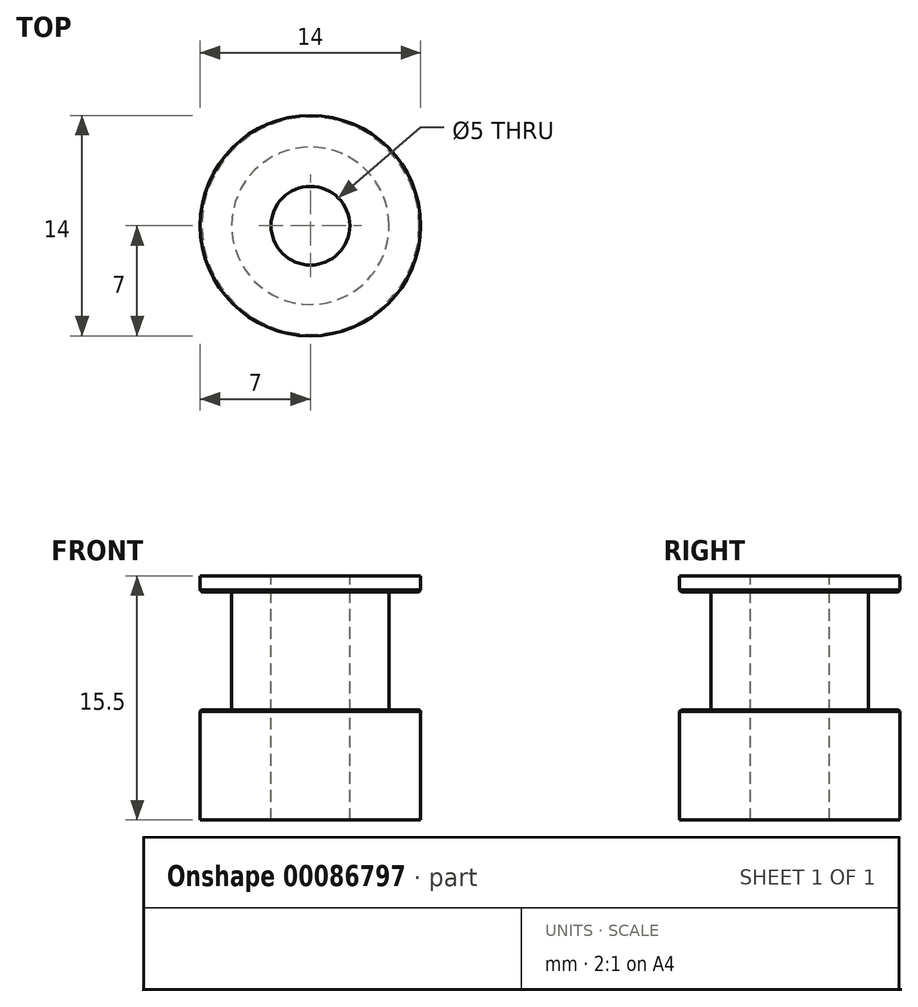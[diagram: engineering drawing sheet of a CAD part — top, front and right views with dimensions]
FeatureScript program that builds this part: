
annotation { "Feature Type Name" : "Feature", "Feature Type Description" : "" }
export const myFeature = defineFeature(function(context is Context, id is Id, definition is map)
    precondition{}
    {
        {
            var Q0;
            Q0=qCreatedBy(makeId("Front.planeOp"),FACE);
            var sketch = newSketch(context, id + "F0", { "sketchPlane" : qUnion([Q0])});
            skLineSegment(sketch, "E0", {"start": v(2.5, 0.06) * mm, "end": v(7, 0.06) * mm});
            skLineSegment(sketch, "E1", {"start": v(7, 0.06) * mm, "end": v(7, 7.06) * mm});
            skLineSegment(sketch, "E2", {"start": v(2.5, 0.06) * mm, "end": v(2.5, 15.56) * mm});
            skLineSegment(sketch, "E3", {"start": v(2.5, 15.56) * mm, "end": v(7, 15.56) * mm});
            skLineSegment(sketch, "E4", {"start": v(7, 15.56) * mm, "end": v(7, 14.56) * mm});
            skLineSegment(sketch, "E5", {"start": v(7, 14.56) * mm, "end": v(5, 14.56) * mm});
            skLineSegment(sketch, "E6", {"start": v(5, 14.56) * mm, "end": v(5, 7.06) * mm});
            skLineSegment(sketch, "E7", {"start": v(5, 7.06) * mm, "end": v(7, 7.06) * mm});
            skLineSegment(sketch, "E8", {"start": v(0, 16.5) * mm, "end": v(0, 0) * mm});
            skSolve(sketch);
        }
        {
            var Q0;
            Q0 = qSketchRegion(id + "F0", true);
            var Q1;
            Q1=sQuery(id+"F0.wireOp",EDGE,"E8");
            revolve(context, id + "F1", {"entities" : qUnion([Q0]), "axis" : qUnion([Q1]), "revolveType" : RevolveType.FULL});
        }
        {
            var Q0;
            Q0=makeQuery(id+"F1.opRevolve","SWEPT_EDGE",EDGE,{"disambiguationData":[OSD([sQuery(id+"F0.wireOp",EDGE,"E4"),sQuery(id+"F0.wireOp",EDGE,"E5")])]});
            var Q1;
            Q1=makeQuery(id+"F1.opRevolve","SWEPT_EDGE",EDGE,{"disambiguationData":[OSD([sQuery(id+"F0.wireOp",EDGE,"E1"),sQuery(id+"F0.wireOp",EDGE,"E7")])]});
            chamfer(context, id + "F2", {"entities" : qUnion([Q0, Q1]), "width" : .1 * mm, "tangentPropagation" : true});
        }
    });
